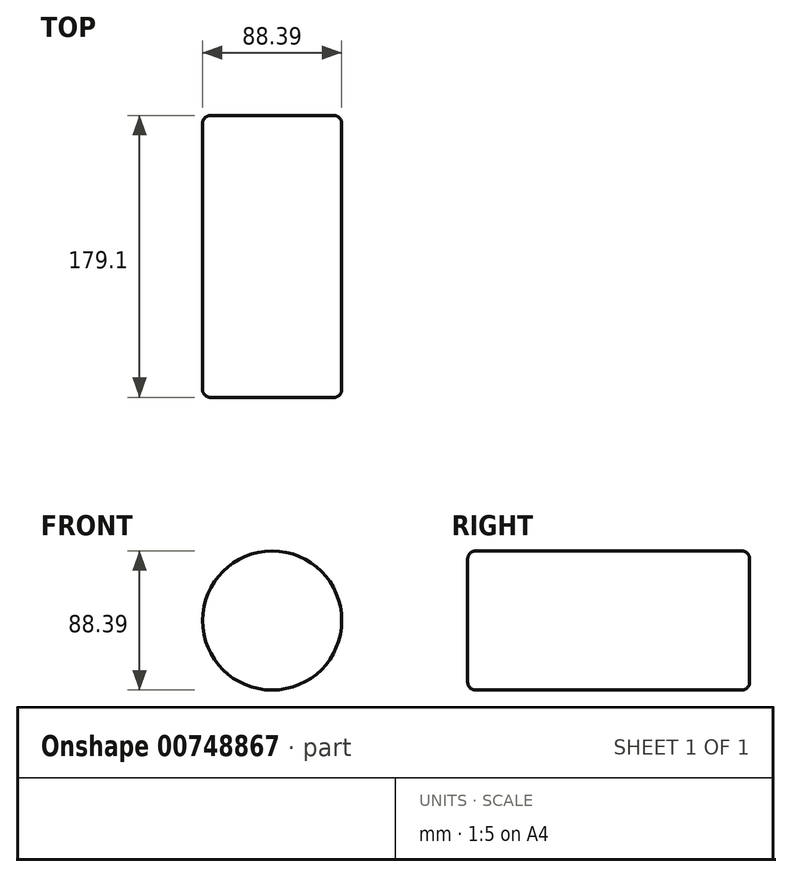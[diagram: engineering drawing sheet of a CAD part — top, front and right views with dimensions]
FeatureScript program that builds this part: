
annotation { "Feature Type Name" : "Feature", "Feature Type Description" : "" }
export const myFeature = defineFeature(function(context is Context, id is Id, definition is map)
    precondition{}
    {
        {
            var Q0;
            Q0=qCreatedBy(makeId("Front.planeOp"),FACE);
            var sketch = newSketch(context, id + "F0", { "sketchPlane" : qUnion([Q0])});
            skCircle(sketch, "E0", {"center": v(170.01, 47.31) * mm, "radius": 44.2 * mm});
            skSolve(sketch);
        }
        {
            var Q0;
            Q0=makeQuery(id+"F0.imprint","IMPRINT",FACE,{"disambiguationData":[TD([[makeQuery(id+"F0.imprint","IMPRINT",EDGE,{"derivedFrom":sQuery(id+"F0.wireOp",EDGE,"E0")}),1.0]])]});
            extrude(context, id + "F1", {"entities" : qUnion([Q0]), "depth" : 179.1 * mm, "offsetDistance" : 25.4 * mm});
        }
        {
            var Q0;
            Q0=makeQuery(id+"F1.opExtrude","SWEPT_FACE",FACE,{"disambiguationData":[OSD([sQuery(id+"F0.wireOp",EDGE,"E0")])]});
            var Q1;
            Q1=makeQuery(id+"F1.opExtrude","CAP_FACE",FACE,{"disambiguationData":[OSD([sQuery(id+"F0.wireOp",EDGE,"E0")])],"isStart":false});
            var Q2;
            Q2=makeQuery(id+"F1.opExtrude","CAP_FACE",FACE,{"disambiguationData":[OSD([sQuery(id+"F0.wireOp",EDGE,"E0")])],"isStart":true});
            fillet(context, id + "F2", {"entities" : qUnion([Q0, Q1, Q2]), "radius" : 5.08 * mm, "tangentPropagation" : true, "allowEdgeOverflow" : false});
        }
    });
